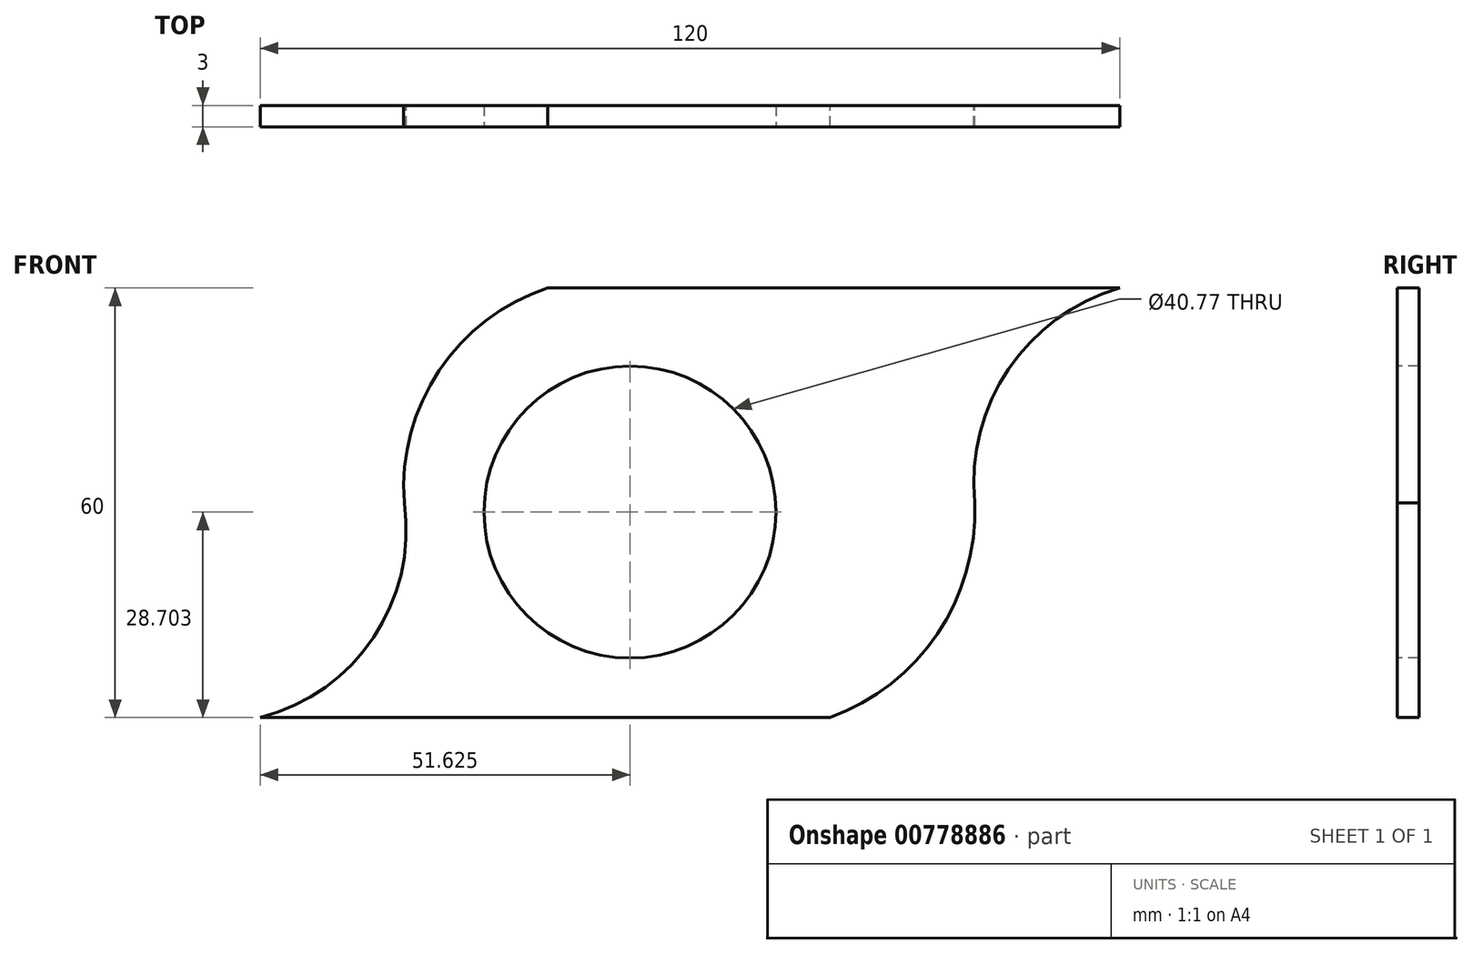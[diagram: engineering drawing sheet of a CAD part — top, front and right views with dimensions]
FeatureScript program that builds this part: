
annotation { "Feature Type Name" : "Feature", "Feature Type Description" : "" }
export const myFeature = defineFeature(function(context is Context, id is Id, definition is map)
    precondition{}
    {
        {
            var Q0;
            Q0=qCreatedBy(makeId("Front.planeOp"),FACE);
            var sketch = newSketch(context, id + "F0", { "sketchPlane" : qUnion([Q0])});
            skArc(sketch, "E0", {"start": v(-59.32, -32.6) * mm, "mid": v(-43.53, -21.44) * mm, "end": v(-39.2, -2.6) * mm});
            skArc(sketch, "E1", {"start": v(-19.16, 27.4) * mm, "mid": v(-34.36, 15.86) * mm, "end": v(-39.2, -2.6) * mm});
            skArc(sketch, "E2", {"start": v(60.68, 27.4) * mm, "mid": v(45.15, 16.05) * mm, "end": v(40.44, -2.6) * mm});
            skArc(sketch, "E3", {"start": v(20.22, -32.6) * mm, "mid": v(35.22, -20.9) * mm, "end": v(40.44, -2.6) * mm});
            skLineSegment(sketch, "E4", {"start": v(20.22, -32.6) * mm, "end": v(-59.32, -32.6) * mm});
            skLineSegment(sketch, "E5", {"start": v(60.68, 27.4) * mm, "end": v(-19.16, 27.4) * mm});
            skSolve(sketch);
        }
        {
            var Q0;
            Q0=makeQuery(id+"F0.imprint","IMPRINT",FACE,{"disambiguationData":[TD([[makeQuery(id+"F0.imprint","IMPRINT",EDGE,{"derivedFrom":sQuery(id+"F0.wireOp",EDGE,"E0")}),-1.0]])]});
            extrude(context, id + "F1", {"entities" : qUnion([Q0]), "depth" : 3 * mm, "offsetDistance" : 25 * mm});
        }
        {
            var Q0;
            Q0=makeQuery(id+"F1.opExtrude","CAP_FACE",FACE,{"disambiguationData":[OSD([sQuery(id+"F0.wireOp",EDGE,"E0"),sQuery(id+"F0.wireOp",EDGE,"E1"),sQuery(id+"F0.wireOp",EDGE,"E2"),sQuery(id+"F0.wireOp",EDGE,"E3"),sQuery(id+"F0.wireOp",EDGE,"E4"),sQuery(id+"F0.wireOp",EDGE,"E5")])],"isStart":false});
            var sketch = newSketch(context, id + "F2", { "sketchPlane" : qUnion([Q0])});
            skCircle(sketch, "E6", {"center": v(-7.7, -3.9) * mm, "radius": 20.39 * mm});
            skCircle(sketch, "E7", {"center": v(25.48, 14.1) * mm, "radius": 6.24 * mm});
            skSolve(sketch);
        }
        {
            var Q0;
            Q0=makeQuery(id+"F2.imprint","IMPRINT",FACE,{"disambiguationData":[TD([[makeQuery(id+"F2.imprint","IMPRINT",EDGE,{"derivedFrom":sQuery(id+"F2.wireOp",EDGE,"E6")}),1.0]])]});
            extrude(context, id + "F3", {"entities" : qUnion([Q0]), "operationType" : NewBodyOperationType.REMOVE, "oppositeDirection" : true, "depth" : 3 * mm, "offsetDistance" : 25 * mm});
        }
    });
